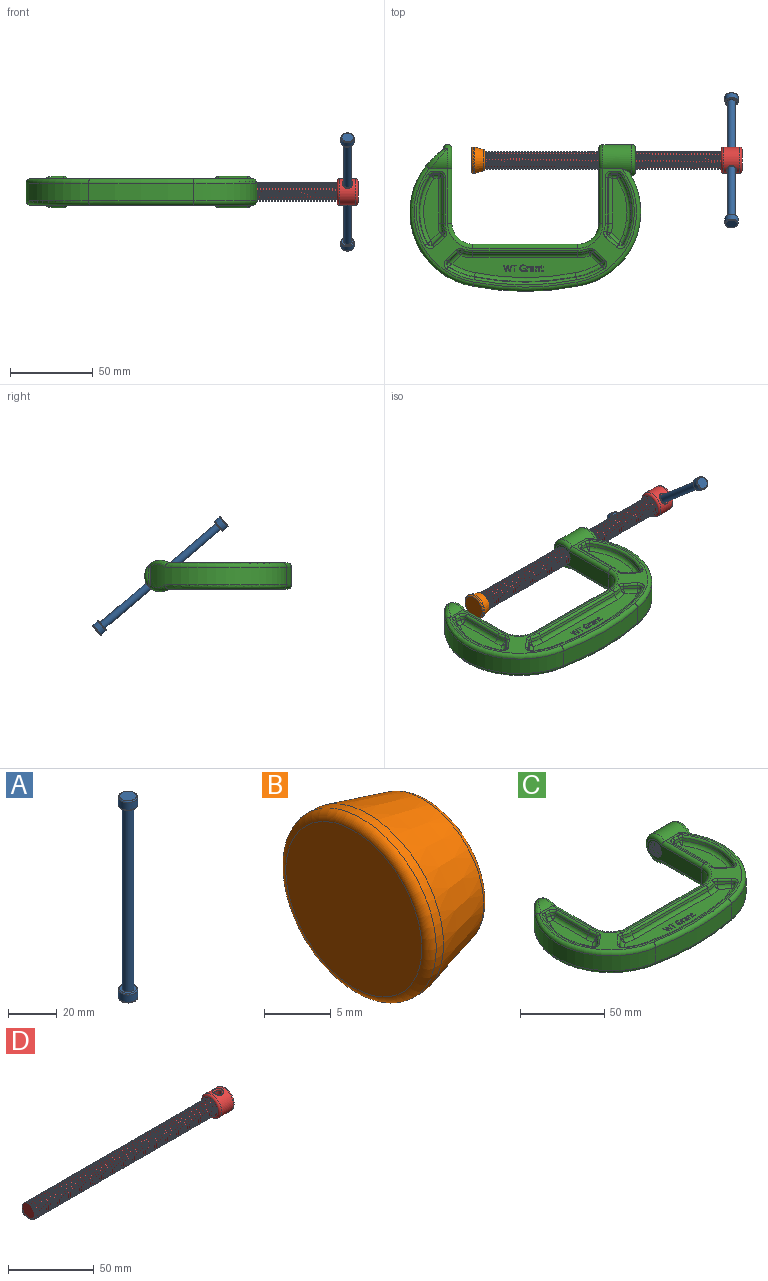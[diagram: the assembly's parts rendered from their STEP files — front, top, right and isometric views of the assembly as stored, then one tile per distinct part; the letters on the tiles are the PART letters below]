
ASSEMBLY  parts=4 mates=5
PART A: 11 faces, bbox 8.6x8.6x101.6 mm
  f0: cylinder r=2.37mm len=92.1mm, axis (0,0,-1), area 1374.3mm2, adj f2,f5
  f1: cylinder r=3.96mm len=7.93mm, axis (0,0,-1), area 93mm2, adj f9,f10
  f2: plane 6.91x6.91mm, normal (0,0,1), area 19.8mm2, adj f0,f10
  f3: plane 6.91x6.91mm, normal (0,0,-1), area 37.5mm2, adj f9
  f4: cylinder r=3.96mm len=7.93mm, axis (0,0,1), area 93mm2, adj f7,f8
  f5: plane 6.91x6.91mm, normal (0,0,-1), area 19.8mm2, adj f0,f8
  f6: plane 6.91x6.91mm, normal (0,0,1), area 37.5mm2, adj f7
  f7: torus R=3.45mm, axis (0,0,1), area 18.9mm2, adj f4,f6
  f8: torus R=3.45mm, axis (0,0,1), area 18.9mm2, adj f4,f5
  f9: torus R=3.45mm, axis (0,0,1), area 18.9mm2, adj f1,f3
  f10: torus R=3.45mm, axis (0,0,-1), area 18.9mm2, adj f1,f2
PART B: 11 faces, bbox 8.6x17.4x17.4 mm
  f0: plane 11.55x11.55mm, normal (1,0,0), area 17.8mm2, adj f4,f5,f6,f7,f10
  f1: cone r=7.94mm half-angle=15deg, axis (-1,0,0), area 269.5mm2, adj f3,f10
  f2: plane 14.35x14.35mm, normal (-1,0,0), area 161.8mm2, adj f9
  f3: cylinder r=7.94mm len=15.88mm, axis (-1,0,0), area 38mm2, adj f1,f9
  f4: bspline ~12.85x11.13mm, area 103.4mm2, adj f0,f6,f7,f8
  f5: bspline ~12.85x11.13mm, area 103.5mm2, adj f0,f6,f7,f8
  f6: cylinder r=5.56mm len=11.13mm, axis (-1,0,0), area 80mm2, adj f0,f4,f5,f8
  f7: cylinder r=4.67mm len=9.35mm, axis (-1,0,0), area 71mm2, adj f0,f4,f5,f8
  f8: plane 10.62x10.49mm, normal (1,0,0), area 82.5mm2, adj f4,f5,f6,f7
  f9: torus R=7.18mm, axis (-1,0,0), area 57.6mm2, adj f2,f3
  f10: torus R=5.65mm, axis (-1,0,0), area 38.1mm2, adj f0,f1
PART C: 361 faces, bbox 147.4x103.2x20.9 mm
  f0: plane 45.34x14.23mm, normal (-1,0,0), area 415.1mm2, adj f2,f9,f14,f15,f123,f358,f359,f360
  f1: plane 14.21x14.2mm, normal (1,0,0), area 70.8mm2, adj f2,f25,f26,f358,f359,f360
  f2: cylinder r=4.67mm len=22.23mm, axis (1,0,0), area 296.6mm2, adj f0,f1,f359,f360
  f3: plane 88.74x13.27mm, normal (0,0,1), area 824mm2, adj f61,f62,f63,f66,f67,f70,f71,f72
  f4: cylinder r=9.53mm len=12.02mm, axis (1,0,0), area 66.9mm2, adj f12,f20,f21
  f5: cylinder r=45.32mm len=82.5mm, axis (0,0,-1), area 1193.7mm2, adj f7,f21,f22,f28,f128,f129
  f6: plane 45.09x13.97mm, normal (1,0,0), area 497.5mm2, adj f11,f19,f20,f127
  f7: cylinder r=160.34mm len=63.5mm, axis (0,0,-1), area 690mm2, adj f5,f8,f24,f131
  f8: cylinder r=45.32mm len=68.35mm, axis (0,0,-1), area 945.9mm2, adj f7,f13,f23,f26,f130
  f9: cylinder r=12.7mm len=12.7mm, axis (0,0,-1), area 215.4mm2, adj f0,f10,f16,f124
  f10: plane 63.5x10.8mm, normal (0,1,0), area 685.5mm2, adj f9,f11,f17,f125
  f11: cylinder r=12.7mm len=12.7mm, axis (0,0,-1), area 215.4mm2, adj f6,f10,f18,f126
  f12: plane 134.76x72.01mm, normal (0,0,1), area 940mm2, adj f4,f13,f15,f16,f17,f18,f19,f21
  f13: cylinder r=9.53mm len=19.05mm, axis (-1,0,0), area 732.8mm2, adj f8,f12,f14,f23,f25,f122,f130
  f14: torus R=6.99mm, axis (1,0,0), area 151.3mm2, adj f0,f13,f15,f123
  f15: cylinder r=2.54mm len=33.67mm, axis (0,1,0), area 132.7mm2, adj f0,f12,f14,f16
  f16: torus R=15.24mm, axis (0,0,1), area 85.4mm2, adj f9,f12,f15,f17
  f17: cylinder r=2.54mm len=63.5mm, axis (1,0,0), area 253.4mm2, adj f10,f12,f16,f18
  f18: torus R=15.24mm, axis (0,0,1), area 85.4mm2, adj f11,f12,f17,f19
  f19: cylinder r=2.54mm len=33.67mm, axis (0,-1,0), area 132.7mm2, adj f6,f12,f18,f20
  f20: torus R=6.99mm, axis (1,0,0), area 189.3mm2, adj f4,f6,f19,f27,f28,f121,f127,f132
  f21: bspline ~15.93x15.22mm, area 60.2mm2, adj f4,f5,f12,f22,f27
  f22: torus R=42.78mm, axis (0,0,1), area 369.7mm2, adj f5,f12,f21,f24
  f23: torus R=42.78mm, axis (0,0,1), area 356.8mm2, adj f8,f12,f13,f24
  f24: torus R=157.8mm, axis (0,0,1), area 253.8mm2, adj f7,f12,f22,f23
  f25: torus R=6.99mm, axis (-1,0,0), area 205.8mm2, adj f1,f13,f26
  f26: bspline ~5.9x2.94mm, area 9.7mm2, adj f1,f8,f25
  f27: bspline ~3.03x2.58mm, area 1.3mm2, adj f20,f21,f28
  f28: bspline ~11.88x1.72mm, area 18.8mm2, adj f5,f20,f27,f132
  f29: plane 27.76x1.74mm, normal (0.97,0,0.26), area 49.9mm2, adj f30,f37,f73,f104
  f30: cone r=17.78mm half-angle=15deg, axis (0,0,-1), area 9.6mm2, adj f29,f31,f75,f103
  f31: cone r=2.54mm half-angle=15deg, axis (0,0,1), area 4mm2, adj f30,f32,f77,f105
  f32: plane 6.61x6.13mm, normal (0.65,0.71,0.26), area 15.4mm2, adj f31,f33,f79,f107
  f33: cone r=2.54mm half-angle=15deg, axis (0,0,1), area 6.5mm2, adj f32,f34,f81,f109
  f34: cone r=40.24mm half-angle=15deg, axis (0,0,1), area 78.6mm2, adj f33,f35,f80,f111
  f35: cone r=2.54mm half-angle=15deg, axis (0,0,1), area 3.5mm2, adj f34,f36,f78,f110
  f36: plane 3.69x1.74mm, normal (0,-0.97,0.26), area 6.6mm2, adj f35,f37,f76,f108
  f37: cone r=2.54mm half-angle=15deg, axis (0,0,1), area 5.7mm2, adj f29,f36,f74,f106
  f38: plane 37.6x9.56mm, normal (0,0,1), area 258.8mm2, adj f73,f75,f76,f79,f80
  f39: cone r=17.78mm half-angle=15deg, axis (0,0,-1), area 12.3mm2, adj f40,f50,f62,f91
  f40: cone r=2.54mm half-angle=15deg, axis (0,0,1), area 4mm2, adj f39,f41,f64,f92
  f41: plane 6.61x6.13mm, normal (0.65,-0.71,0.26), area 15.4mm2, adj f40,f42,f66,f94
  f42: cone r=2.54mm half-angle=15deg, axis (0,0,1), area 6.5mm2, adj f41,f43,f68,f96
  f43: cone r=40.24mm half-angle=15deg, axis (0,0,1), area 30.8mm2, adj f42,f44,f70,f98
  f44: cone r=155.26mm half-angle=15deg, axis (0,0,1), area 111.4mm2, adj f43,f45,f72,f100
  f45: cone r=40.24mm half-angle=15deg, axis (0,0,1), area 30.8mm2, adj f44,f46,f71,f102
  f46: cone r=2.54mm half-angle=15deg, axis (0,0,1), area 6.5mm2, adj f45,f47,f69,f101
  f47: plane 6.61x6.13mm, normal (-0.65,-0.71,0.26), area 15.4mm2, adj f46,f48,f67,f99
  f48: cone r=2.54mm half-angle=15deg, axis (0,0,1), area 4mm2, adj f47,f49,f65,f97
  f49: cone r=17.78mm half-angle=15deg, axis (0,0,-1), area 12.3mm2, adj f48,f50,f63,f95
  f50: plane 63.5x1.74mm, normal (0,-0.97,0.26), area 114.2mm2, adj f39,f49,f61,f93
  f51: plane 27.76x1.74mm, normal (-0.97,0,0.26), area 49.9mm2, adj f52,f59,f90,f120
  f52: cone r=2.54mm half-angle=15deg, axis (0,0,1), area 5.7mm2, adj f51,f53,f89,f119
  f53: plane 3.69x1.74mm, normal (0,-0.97,0.26), area 6.6mm2, adj f52,f54,f87,f117
  f54: cone r=2.54mm half-angle=15deg, axis (0,0,1), area 3.5mm2, adj f53,f55,f85,f115
  f55: cone r=40.24mm half-angle=15deg, axis (0,0,1), area 78.6mm2, adj f54,f56,f83,f113
  f56: cone r=2.54mm half-angle=15deg, axis (0,0,1), area 6.5mm2, adj f55,f57,f82,f112
  f57: plane 6.61x6.13mm, normal (-0.65,0.71,0.26), area 15.4mm2, adj f56,f58,f84,f114
  f58: cone r=2.54mm half-angle=15deg, axis (0,0,1), area 4mm2, adj f57,f59,f86,f116
  f59: cone r=17.78mm half-angle=15deg, axis (0,0,-1), area 9.6mm2, adj f51,f58,f88,f118
  f60: plane 37.6x9.56mm, normal (0,0,1), area 258.8mm2, adj f83,f84,f87,f88,f90
  f61: cylinder r=2.54mm len=63.5mm, axis (-1,0,0), area 211.1mm2, adj f3,f50,f62,f63
  f62: torus R=21mm, axis (0,0,1), area 23.7mm2, adj f3,f39,f61,f64
  f63: torus R=21mm, axis (0,0,1), area 23.7mm2, adj f3,f49,f61,f65
  f64: bspline ~2.55x1.88mm, area 2.4mm2, adj f40,f62,f66
  f65: bspline ~2.55x1.88mm, area 2.4mm2, adj f48,f63,f67
  f66: cylinder r=2.54mm len=7.96mm, axis (-0.74,-0.68,0), area 26.3mm2, adj f3,f41,f64,f68
  f67: cylinder r=2.54mm len=7.96mm, axis (0.74,-0.68,0), area 26.3mm2, adj f3,f47,f65,f69
  f68: bspline ~2.81x2.78mm, area 3.9mm2, adj f42,f66,f70
  f69: bspline ~2.81x2.78mm, area 3.9mm2, adj f46,f67,f71
  f70: torus R=37.02mm, axis (0,0,1), area 53.8mm2, adj f3,f43,f68,f72
  f71: torus R=37.02mm, axis (0,0,1), area 53.8mm2, adj f3,f45,f69,f72
  f72: torus R=152.04mm, axis (0,0,1), area 204.4mm2, adj f3,f44,f70,f71
  f73: cylinder r=2.54mm len=27.76mm, axis (0,-1,0), area 91.1mm2, adj f29,f38,f74,f75
  f74: bspline ~2.45x2.45mm, area 3.4mm2, adj f37,f73,f76
  f75: torus R=21mm, axis (0,0,1), area 18.2mm2, adj f30,f38,f73,f77
  f76: cylinder r=2.54mm len=3.69mm, axis (1,0,0), area 10.5mm2, adj f36,f38,f74,f78
  f77: bspline ~2.53x1.88mm, area 2.4mm2, adj f31,f75,f79
  f78: bspline ~2.45x1.88mm, area 2.1mm2, adj f35,f76,f80
  f79: cylinder r=2.54mm len=7.96mm, axis (0.74,-0.68,0), area 26.3mm2, adj f32,f38,f77,f81
  f80: torus R=37.02mm, axis (0,0,1), area 138.6mm2, adj f34,f38,f78,f81
  f81: bspline ~2.8x2.75mm, area 4mm2, adj f33,f79,f80
  f82: bspline ~2.8x2.75mm, area 3.9mm2, adj f56,f83,f84
  f83: torus R=37.02mm, axis (0,0,1), area 138.6mm2, adj f55,f60,f82,f85
  f84: cylinder r=2.54mm len=7.96mm, axis (-0.74,-0.68,0), area 26.3mm2, adj f57,f60,f82,f86
  f85: bspline ~2.45x1.88mm, area 2.1mm2, adj f54,f83,f87
  f86: bspline ~2.53x1.88mm, area 2.4mm2, adj f58,f84,f88
  f87: cylinder r=2.54mm len=3.69mm, axis (1,0,0), area 10.5mm2, adj f53,f60,f85,f89
  f88: torus R=21mm, axis (0,0,1), area 18.2mm2, adj f59,f60,f86,f90
  f89: bspline ~2.45x2.45mm, area 3.4mm2, adj f52,f87,f90
  f90: cylinder r=2.54mm len=27.76mm, axis (0,1,0), area 91.1mm2, adj f51,f60,f88,f89
  f91: torus R=16.61mm, axis (0,0,1), area 13mm2, adj f12,f39,f92,f93
  f92: torus R=3.71mm, axis (0,0,1), area 6.3mm2, adj f12,f40,f91,f94
  f93: cylinder r=1.52mm len=63.5mm, axis (1,0,0), area 126.7mm2, adj f12,f50,f91,f95
  f94: cylinder r=1.52mm len=7.29mm, axis (0.74,0.68,0), area 17.1mm2, adj f12,f41,f92,f96
  f95: torus R=16.61mm, axis (0,0,1), area 13mm2, adj f12,f49,f93,f97
  f96: torus R=3.71mm, axis (0,0,1), area 10.3mm2, adj f12,f42,f94,f98
  f97: torus R=3.71mm, axis (0,0,1), area 6.3mm2, adj f12,f48,f95,f99
  f98: torus R=41.41mm, axis (0,0,1), area 34.9mm2, adj f12,f43,f96,f100
  f99: cylinder r=1.52mm len=7.29mm, axis (-0.74,0.68,0), area 17.1mm2, adj f12,f47,f97,f101
  f100: torus R=156.43mm, axis (0,0,1), area 124.1mm2, adj f12,f44,f98,f102
  f101: torus R=3.71mm, axis (0,0,1), area 10.3mm2, adj f12,f46,f99,f102
  f102: torus R=41.41mm, axis (0,0,1), area 34.9mm2, adj f12,f45,f100,f101
  f103: torus R=16.61mm, axis (0,0,1), area 10.1mm2, adj f12,f30,f104,f105
  f104: cylinder r=1.52mm len=27.76mm, axis (0,1,0), area 55.4mm2, adj f12,f29,f103,f106
  f105: torus R=3.71mm, axis (0,0,1), area 6.3mm2, adj f12,f31,f103,f107
  f106: torus R=3.71mm, axis (0,0,1), area 8.9mm2, adj f12,f37,f104,f108
  f107: cylinder r=1.52mm len=7.29mm, axis (-0.74,0.68,0), area 17.1mm2, adj f12,f32,f105,f109
  f108: cylinder r=1.52mm len=3.69mm, axis (-1,0,0), area 7.4mm2, adj f12,f36,f106,f110
  f109: torus R=3.71mm, axis (0,0,1), area 10.3mm2, adj f12,f33,f107,f111
  f110: torus R=3.71mm, axis (0,0,1), area 5.5mm2, adj f12,f35,f108,f111
  f111: torus R=41.41mm, axis (0,0,1), area 89mm2, adj f12,f34,f109,f110
  f112: torus R=3.71mm, axis (0,0,1), area 10.3mm2, adj f12,f56,f113,f114
  f113: torus R=41.41mm, axis (0,0,1), area 89mm2, adj f12,f55,f112,f115
  f114: cylinder r=1.52mm len=7.29mm, axis (0.74,0.68,0), area 17.1mm2, adj f12,f57,f112,f116
  f115: torus R=3.71mm, axis (0,0,1), area 5.5mm2, adj f12,f54,f113,f117
  f116: torus R=3.71mm, axis (0,0,1), area 6.3mm2, adj f12,f58,f114,f118
  f117: cylinder r=1.52mm len=3.69mm, axis (-1,0,0), area 7.4mm2, adj f12,f53,f115,f119
  f118: torus R=16.61mm, axis (0,0,1), area 10.1mm2, adj f12,f59,f116,f120
  f119: torus R=3.71mm, axis (0,0,1), area 8.9mm2, adj f12,f52,f117,f120
  f120: cylinder r=1.52mm len=27.76mm, axis (0,-1,0), area 55.4mm2, adj f12,f51,f118,f119
  f121: cylinder r=9.53mm len=12.02mm, axis (1,0,0), area 66.9mm2, adj f20,f122,f128
  f122: plane 134.76x72.01mm, normal (0,0,-1), area 940mm2, adj f13,f121,f123,f124,f125,f126,f127,f128
  f123: cylinder r=2.54mm len=33.67mm, axis (0,1,0), area 132.7mm2, adj f0,f14,f122,f124
  f124: torus R=15.24mm, axis (0,0,-1), area 85.4mm2, adj f9,f122,f123,f125
  f125: cylinder r=2.54mm len=63.5mm, axis (1,0,0), area 253.4mm2, adj f10,f122,f124,f126
  f126: torus R=15.24mm, axis (0,0,-1), area 85.4mm2, adj f11,f122,f125,f127
  f127: cylinder r=2.54mm len=33.67mm, axis (0,-1,0), area 132.7mm2, adj f6,f20,f122,f126
  f128: bspline ~15.93x15.22mm, area 60.2mm2, adj f5,f121,f122,f129,f132
  f129: torus R=42.78mm, axis (0,0,-1), area 369.7mm2, adj f5,f122,f128,f131
  f130: torus R=42.78mm, axis (0,0,-1), area 356.8mm2, adj f8,f13,f122,f131
  f131: torus R=157.8mm, axis (0,0,-1), area 253.8mm2, adj f7,f122,f129,f130
  f132: bspline ~3.03x2.58mm, area 1.3mm2, adj f20,f28,f128
  f133: plane 27.76x1.74mm, normal (0.97,0,-0.26), area 49.9mm2, adj f134,f141,f178,f209
  f134: cone r=17.78mm half-angle=15deg, axis (0,0,1), area 9.6mm2, adj f133,f135,f180,f208
  f135: cone r=2.54mm half-angle=15deg, axis (0,0,-1), area 4mm2, adj f134,f136,f182,f210
  f136: plane 6.61x6.13mm, normal (0.65,0.71,-0.26), area 15.4mm2, adj f135,f137,f184,f212
  f137: cone r=2.54mm half-angle=15deg, axis (0,0,-1), area 6.5mm2, adj f136,f138,f186,f214
  f138: cone r=40.24mm half-angle=15deg, axis (0,0,-1), area 78.6mm2, adj f137,f139,f185,f216
  f139: cone r=2.54mm half-angle=15deg, axis (0,0,-1), area 3.5mm2, adj f138,f140,f183,f215
  f140: plane 3.69x1.74mm, normal (0,-0.97,-0.26), area 6.6mm2, adj f139,f141,f181,f213
  f141: cone r=2.54mm half-angle=15deg, axis (0,0,-1), area 5.7mm2, adj f133,f140,f179,f211
  f142: plane 37.6x9.56mm, normal (0,0,-1), area 258.8mm2, adj f178,f180,f181,f184,f185
  f143: cone r=17.78mm half-angle=15deg, axis (0,0,1), area 12.3mm2, adj f144,f154,f167,f196
  f144: cone r=2.54mm half-angle=15deg, axis (0,0,-1), area 4mm2, adj f143,f145,f169,f197
  f145: plane 6.61x6.13mm, normal (0.65,-0.71,-0.26), area 15.4mm2, adj f144,f146,f171,f199
  f146: cone r=2.54mm half-angle=15deg, axis (0,0,-1), area 6.5mm2, adj f145,f147,f173,f201
  f147: cone r=40.24mm half-angle=15deg, axis (0,0,-1), area 30.8mm2, adj f146,f148,f175,f203
  f148: cone r=155.26mm half-angle=15deg, axis (0,0,-1), area 111.4mm2, adj f147,f149,f177,f205
  f149: cone r=40.24mm half-angle=15deg, axis (0,0,-1), area 30.8mm2, adj f148,f150,f176,f207
  f150: cone r=2.54mm half-angle=15deg, axis (0,0,-1), area 6.5mm2, adj f149,f151,f174,f206
  f151: plane 6.61x6.13mm, normal (-0.65,-0.71,-0.26), area 15.4mm2, adj f150,f152,f172,f204
  f152: cone r=2.54mm half-angle=15deg, axis (0,0,-1), area 4mm2, adj f151,f153,f170,f202
  f153: cone r=17.78mm half-angle=15deg, axis (0,0,1), area 12.3mm2, adj f152,f154,f168,f200
  f154: plane 63.5x1.74mm, normal (0,-0.97,-0.26), area 114.2mm2, adj f143,f153,f166,f198
  f155: plane 88.74x13.27mm, normal (0,0,-1), area 849.9mm2, adj f166,f167,f168,f171,f172,f175,f176,f177
  f156: plane 27.76x1.74mm, normal (-0.97,0,-0.26), area 49.9mm2, adj f157,f164,f195,f225
  f157: cone r=2.54mm half-angle=15deg, axis (0,0,-1), area 5.7mm2, adj f156,f158,f194,f224
  f158: plane 3.69x1.74mm, normal (0,-0.97,-0.26), area 6.6mm2, adj f157,f159,f192,f222
  f159: cone r=2.54mm half-angle=15deg, axis (0,0,-1), area 3.5mm2, adj f158,f160,f190,f220
  f160: cone r=40.24mm half-angle=15deg, axis (0,0,-1), area 78.6mm2, adj f159,f161,f188,f218
  f161: cone r=2.54mm half-angle=15deg, axis (0,0,-1), area 6.5mm2, adj f160,f162,f187,f217
  f162: plane 6.61x6.13mm, normal (-0.65,0.71,-0.26), area 15.4mm2, adj f161,f163,f189,f219
  f163: cone r=2.54mm half-angle=15deg, axis (0,0,-1), area 4mm2, adj f162,f164,f191,f221
  f164: cone r=17.78mm half-angle=15deg, axis (0,0,1), area 9.6mm2, adj f156,f163,f193,f223
  f165: plane 37.6x9.56mm, normal (0,0,-1), area 258.8mm2, adj f188,f189,f192,f193,f195
  f166: cylinder r=2.54mm len=63.5mm, axis (-1,0,0), area 211.1mm2, adj f154,f155,f167,f168
  f167: torus R=21mm, axis (0,0,-1), area 23.7mm2, adj f143,f155,f166,f169
  f168: torus R=21mm, axis (0,0,-1), area 23.7mm2, adj f153,f155,f166,f170
  f169: bspline ~2.55x1.88mm, area 2.4mm2, adj f144,f167,f171
  f170: bspline ~2.55x1.88mm, area 2.4mm2, adj f152,f168,f172
  f171: cylinder r=2.54mm len=7.96mm, axis (-0.74,-0.68,0), area 26.3mm2, adj f145,f155,f169,f173
  f172: cylinder r=2.54mm len=7.96mm, axis (0.74,-0.68,0), area 26.3mm2, adj f151,f155,f170,f174
  f173: bspline ~2.81x2.78mm, area 3.9mm2, adj f146,f171,f175
  f174: bspline ~2.81x2.78mm, area 3.9mm2, adj f150,f172,f176
  f175: torus R=37.02mm, axis (0,0,-1), area 53.8mm2, adj f147,f155,f173,f177
  f176: torus R=37.02mm, axis (0,0,-1), area 53.8mm2, adj f149,f155,f174,f177
  f177: torus R=152.04mm, axis (0,0,-1), area 204.4mm2, adj f148,f155,f175,f176
  f178: cylinder r=2.54mm len=27.76mm, axis (0,-1,0), area 91.1mm2, adj f133,f142,f179,f180
  f179: bspline ~2.45x2.45mm, area 3.4mm2, adj f141,f178,f181
  f180: torus R=21mm, axis (0,0,-1), area 18.2mm2, adj f134,f142,f178,f182
  f181: cylinder r=2.54mm len=3.69mm, axis (1,0,0), area 10.5mm2, adj f140,f142,f179,f183
  f182: bspline ~2.53x1.88mm, area 2.4mm2, adj f135,f180,f184
  f183: bspline ~2.45x1.88mm, area 2.1mm2, adj f139,f181,f185
  f184: cylinder r=2.54mm len=7.96mm, axis (0.74,-0.68,0), area 26.3mm2, adj f136,f142,f182,f186
  f185: torus R=37.02mm, axis (0,0,-1), area 138.6mm2, adj f138,f142,f183,f186
  f186: bspline ~2.8x2.75mm, area 4mm2, adj f137,f184,f185
  f187: bspline ~2.8x2.75mm, area 3.9mm2, adj f161,f188,f189
  f188: torus R=37.02mm, axis (0,0,-1), area 138.6mm2, adj f160,f165,f187,f190
  f189: cylinder r=2.54mm len=7.96mm, axis (-0.74,-0.68,0), area 26.3mm2, adj f162,f165,f187,f191
  f190: bspline ~2.45x1.88mm, area 2.1mm2, adj f159,f188,f192
  f191: bspline ~2.53x1.88mm, area 2.4mm2, adj f163,f189,f193
  f192: cylinder r=2.54mm len=3.69mm, axis (1,0,0), area 10.5mm2, adj f158,f165,f190,f194
  f193: torus R=21mm, axis (0,0,-1), area 18.2mm2, adj f164,f165,f191,f195
  f194: bspline ~2.45x2.45mm, area 3.4mm2, adj f157,f192,f195
  f195: cylinder r=2.54mm len=27.76mm, axis (0,1,0), area 91.1mm2, adj f156,f165,f193,f194
  f196: torus R=16.61mm, axis (0,0,-1), area 13mm2, adj f122,f143,f197,f198
  f197: torus R=3.71mm, axis (0,0,-1), area 6.3mm2, adj f122,f144,f196,f199
  f198: cylinder r=1.52mm len=63.5mm, axis (1,0,0), area 126.7mm2, adj f122,f154,f196,f200
  f199: cylinder r=1.52mm len=7.29mm, axis (0.74,0.68,0), area 17.1mm2, adj f122,f145,f197,f201
  f200: torus R=16.61mm, axis (0,0,-1), area 13mm2, adj f122,f153,f198,f202
  f201: torus R=3.71mm, axis (0,0,-1), area 10.3mm2, adj f122,f146,f199,f203
  f202: torus R=3.71mm, axis (0,0,-1), area 6.3mm2, adj f122,f152,f200,f204
  f203: torus R=41.41mm, axis (0,0,-1), area 34.9mm2, adj f122,f147,f201,f205
  f204: cylinder r=1.52mm len=7.29mm, axis (-0.74,0.68,0), area 17.1mm2, adj f122,f151,f202,f206
  f205: torus R=156.43mm, axis (0,0,-1), area 124.1mm2, adj f122,f148,f203,f207
  f206: torus R=3.71mm, axis (0,0,-1), area 10.3mm2, adj f122,f150,f204,f207
  f207: torus R=41.41mm, axis (0,0,-1), area 34.9mm2, adj f122,f149,f205,f206
  f208: torus R=16.61mm, axis (0,0,-1), area 10.1mm2, adj f122,f134,f209,f210
  f209: cylinder r=1.52mm len=27.76mm, axis (0,1,0), area 55.4mm2, adj f122,f133,f208,f211
  f210: torus R=3.71mm, axis (0,0,-1), area 6.3mm2, adj f122,f135,f208,f212
  f211: torus R=3.71mm, axis (0,0,-1), area 8.9mm2, adj f122,f141,f209,f213
  f212: cylinder r=1.52mm len=7.29mm, axis (-0.74,0.68,0), area 17.1mm2, adj f122,f136,f210,f214
  f213: cylinder r=1.52mm len=3.69mm, axis (-1,0,0), area 7.4mm2, adj f122,f140,f211,f215
  f214: torus R=3.71mm, axis (0,0,-1), area 10.3mm2, adj f122,f137,f212,f216
  f215: torus R=3.71mm, axis (0,0,-1), area 5.5mm2, adj f122,f139,f213,f216
  f216: torus R=41.41mm, axis (0,0,-1), area 89mm2, adj f122,f138,f214,f215
  f217: torus R=3.71mm, axis (0,0,-1), area 10.3mm2, adj f122,f161,f218,f219
  f218: torus R=41.41mm, axis (0,0,-1), area 89mm2, adj f122,f160,f217,f220
  f219: cylinder r=1.52mm len=7.29mm, axis (0.74,0.68,0), area 17.1mm2, adj f122,f162,f217,f221
  f220: torus R=3.71mm, axis (0,0,-1), area 5.5mm2, adj f122,f159,f218,f222
  f221: torus R=3.71mm, axis (0,0,-1), area 6.3mm2, adj f122,f163,f219,f223
  f222: cylinder r=1.52mm len=3.69mm, axis (-1,0,0), area 7.4mm2, adj f122,f158,f220,f224
  f223: torus R=16.61mm, axis (0,0,-1), area 10.1mm2, adj f122,f164,f221,f225
  f224: torus R=3.71mm, axis (0,0,-1), area 8.9mm2, adj f122,f157,f222,f225
  f225: cylinder r=1.52mm len=27.76mm, axis (0,-1,0), area 55.4mm2, adj f122,f156,f223,f224
  f226: plane 0.76x0.46mm, normal (0,1,0), area 0.3mm2, adj f3,f227,f233,f234
  f227: plane 3.52x0.76mm, normal (-1,0,0), area 2.7mm2, adj f3,f226,f228,f234
  f228: plane 1.24x0.76mm, normal (0,1,0), area 0.9mm2, adj f3,f227,f229,f234
  f229: plane 0.76x0.41mm, normal (-1,0,0), area 0.3mm2, adj f3,f228,f230,f234
  f230: plane 2.94x0.76mm, normal (0,-1,0), area 2.2mm2, adj f3,f229,f231,f234
  f231: plane 0.76x0.41mm, normal (1,0,0), area 0.3mm2, adj f3,f230,f232,f234
  f232: plane 1.24x0.76mm, normal (0,1,0), area 0.9mm2, adj f3,f231,f233,f234
  f233: plane 3.52x0.76mm, normal (1,0,0), area 2.7mm2, adj f3,f226,f232,f234
  f234: plane 3.92x2.94mm, normal (0,0,1), area 2.8mm2, adj f226,f227,f228,f229,f230,f231,f232,f233
  f235: plane 1.33x0.76mm, normal (0,-1,0), area 1mm2, adj f3,f236,f254,f255
  f236: plane 0.76x0.41mm, normal (1,0,0), area 0.3mm2, adj f3,f235,f237,f255
  f237: plane 0.88x0.76mm, normal (0,1,0), area 0.7mm2, adj f3,f236,f238,f255
  f238: plane 1.21x0.76mm, normal (1,0,0), area 0.9mm2, adj f3,f237,f239,f255
  f239: extruded ~0.8x0.76mm, area 0.6mm2, adj f3,f238,f240,f255
  f240: extruded ~1.14x0.76mm, area 0.9mm2, adj f3,f239,f241,f255
  f241: extruded ~1.2x0.76mm, area 1mm2, adj f3,f240,f242,f255
  f242: extruded ~1.18x0.76mm, area 1mm2, adj f3,f241,f243,f255
  f243: extruded ~1.12x0.76mm, area 0.9mm2, adj f3,f242,f244,f255
  f244: extruded ~1.02x0.76mm, area 0.8mm2, adj f3,f243,f245,f255
  f245: plane 0.76x0.4mm, normal (-0.92,0.4,0), area 0.3mm2, adj f3,f244,f246,f255
  f246: extruded ~1.17x0.76mm, area 0.9mm2, adj f3,f245,f247,f255
  f247: extruded ~1.08x0.76mm, area 0.9mm2, adj f3,f246,f248,f255
  f248: extruded ~0.76x0.71mm, area 0.8mm2, adj f3,f247,f249,f255
  f249: extruded ~1.07x0.76mm, area 0.8mm2, adj f3,f248,f250,f255
  f250: extruded ~1.49x0.76mm, area 1.2mm2, adj f3,f249,f251,f255
  f251: extruded ~1.39x0.76mm, area 1.2mm2, adj f3,f250,f252,f255
  f252: extruded ~0.76x0.75mm, area 0.6mm2, adj f3,f251,f253,f255
  f253: extruded ~0.76x0.63mm, area 0.5mm2, adj f3,f252,f254,f255
  f254: plane 1.91x0.76mm, normal (-1,0,0), area 1.5mm2, adj f3,f235,f253,f255
  f255: plane 4.03x3.26mm, normal (0,0,1), area 4.7mm2, adj f235,f236,f237,f238,f239,f240,f241,f242
  f256: extruded ~0.76x0.35mm, area 0.3mm2, adj f3,f257,f268,f269
  f257: extruded ~0.76x0.51mm, area 0.4mm2, adj f3,f256,f258,f269
  f258: extruded ~0.76x0.44mm, area 0.5mm2, adj f3,f257,f259,f269
  f259: plane 0.76x0.02mm, normal (0,-1,0), area 0mm2, adj f3,f258,f260,f269
  f260: plane 0.76x0.54mm, normal (-1,-0.09,0), area 0.4mm2, adj f3,f259,f261,f269
  f261: plane 0.76x0.37mm, normal (0,-1,0), area 0.3mm2, adj f3,f260,f262,f269
  f262: plane 2.94x0.76mm, normal (1,0,0), area 2.2mm2, adj f3,f261,f263,f269
  f263: plane 0.76x0.45mm, normal (0,1,0), area 0.3mm2, adj f3,f262,f264,f269
  f264: plane 1.58x0.76mm, normal (-1,0,0), area 1.2mm2, adj f3,f263,f265,f269
  f265: extruded ~0.76x0.72mm, area 0.6mm2, adj f3,f264,f266,f269
  f266: extruded ~0.76x0.61mm, area 0.5mm2, adj f3,f265,f267,f269
  f267: extruded ~0.76x0.32mm, area 0.2mm2, adj f3,f266,f268,f269
  f268: plane 0.76x0.41mm, normal (-0.99,0.15,0), area 0.3mm2, adj f3,f256,f267,f269
  f269: plane 2.99x1.69mm, normal (0,0,1), area 1.8mm2, adj f256,f257,f258,f259,f260,f261,f262,f263
  f270: plane 1.9x0.76mm, normal (1,0,0), area 1.4mm2, adj f3,f271,f286,f287
  f271: plane 0.76x0.45mm, normal (0,1,0), area 0.3mm2, adj f3,f270,f272,f287
  f272: plane 1.92x0.76mm, normal (-1,0,0), area 1.5mm2, adj f3,f271,f273,f287
  f273: extruded ~0.82x0.76mm, area 0.7mm2, adj f3,f272,f274,f287
  f274: extruded ~0.8x0.76mm, area 0.7mm2, adj f3,f273,f275,f287
  f275: extruded ~0.76x0.55mm, area 0.4mm2, adj f3,f274,f276,f287
  f276: extruded ~0.76x0.38mm, area 0.4mm2, adj f3,f275,f277,f287
  f277: plane 0.76x0.02mm, normal (0,-1,0), area 0mm2, adj f3,f276,f278,f287
  f278: plane 0.76x0.4mm, normal (-0.98,-0.18,0), area 0.3mm2, adj f3,f277,f279,f287
  f279: plane 0.76x0.36mm, normal (0,-1,0), area 0.3mm2, adj f3,f278,f280,f287
  f280: plane 2.94x0.76mm, normal (1,0,0), area 2.2mm2, adj f3,f279,f281,f287
  f281: plane 0.76x0.45mm, normal (0,1,0), area 0.3mm2, adj f3,f280,f282,f287
  f282: plane 1.54x0.76mm, normal (-1,0,0), area 1.2mm2, adj f3,f281,f283,f287
  f283: extruded ~0.82x0.76mm, area 0.7mm2, adj f3,f282,f284,f287
  f284: extruded ~0.76x0.68mm, area 0.6mm2, adj f3,f283,f285,f287
  f285: extruded ~0.76x0.51mm, area 0.4mm2, adj f3,f284,f286,f287
  f286: extruded ~0.76x0.54mm, area 0.4mm2, adj f3,f270,f285,f287
  f287: plane 2.99x2.46mm, normal (0,0,1), area 3.1mm2, adj f270,f271,f272,f273,f274,f275,f276,f277
  f288: extruded ~0.76x0.23mm, area 0.2mm2, adj f3,f289,f306,f307
  f289: extruded ~0.76x0.35mm, area 0.3mm2, adj f3,f288,f290,f307
  f290: extruded ~0.76x0.41mm, area 0.3mm2, adj f3,f289,f291,f307
  f291: plane 1.73x0.76mm, normal (-1,0,0), area 1.3mm2, adj f3,f290,f292,f307
  f292: plane 0.85x0.76mm, normal (0,1,0), area 0.7mm2, adj f3,f291,f293,f307
  f293: plane 0.76x0.35mm, normal (-1,0,0), area 0.3mm2, adj f3,f292,f294,f307
  f294: plane 0.85x0.76mm, normal (0,-1,0), area 0.7mm2, adj f3,f293,f295,f307
  f295: plane 0.76x0.68mm, normal (-1,0,0), area 0.5mm2, adj f3,f294,f296,f307
  f296: plane 0.76x0.26mm, normal (0,-1,0), area 0.2mm2, adj f3,f295,f297,f307
  f297: plane 0.76x0.63mm, normal (0.96,-0.29,0), area 0.5mm2, adj f3,f296,f298,f307
  f298: plane 0.76x0.42mm, normal (0.4,-0.92,0), area 0.4mm2, adj f3,f297,f299,f307
  f299: plane 0.76x0.21mm, normal (1,0,0), area 0.2mm2, adj f3,f298,f300,f307
  f300: plane 0.76x0.42mm, normal (0,1,0), area 0.3mm2, adj f3,f299,f301,f307
  f301: plane 1.75x0.76mm, normal (1,0,0), area 1.3mm2, adj f3,f300,f302,f307
  f302: extruded ~0.9x0.85mm, area 1.1mm2, adj f3,f301,f303,f307
  f303: extruded ~0.76x0.25mm, area 0.2mm2, adj f3,f302,f304,f307
  f304: extruded ~0.76x0.21mm, area 0.2mm2, adj f3,f303,f305,f307
  f305: plane 0.76x0.34mm, normal (-1,0,0), area 0.3mm2, adj f3,f304,f306,f307
  f306: extruded ~0.76x0.17mm, area 0.1mm2, adj f3,f288,f305,f307
  f307: plane 3.68x1.74mm, normal (0,0,1), area 2.2mm2, adj f288,f289,f290,f291,f292,f293,f294,f295
  f308: extruded ~0.76x0.65mm, area 0.5mm2, adj f309,f334,f335,f357
  f309: extruded ~0.76x0.41mm, area 0.3mm2, adj f308,f310,f335,f357
  f310: extruded ~0.76x0.37mm, area 0.3mm2, adj f309,f311,f335,f357
  f311: extruded ~0.76x0.45mm, area 0.4mm2, adj f310,f312,f335,f357
  f312: extruded ~0.77x0.76mm, area 0.6mm2, adj f311,f313,f335,f357
  f313: plane 0.76x0.45mm, normal (-0.04,1,0), area 0.3mm2, adj f312,f314,f335,f357
  f314: plane 0.76x0.27mm, normal (1,0,0), area 0.2mm2, adj f313,f334,f335,f357
  f315: plane 0.76x0.42mm, normal (0.98,0.21,0), area 0.3mm2, adj f3,f316,f333,f335
  f316: plane 0.76x0.33mm, normal (0,1,0), area 0.3mm2, adj f3,f315,f317,f335
  f317: plane 2.01x0.76mm, normal (-1,0,0), area 1.5mm2, adj f3,f316,f318,f335
  f318: extruded ~0.76x0.75mm, area 0.6mm2, adj f3,f317,f319,f335
  f319: extruded ~0.78x0.76mm, area 0.6mm2, adj f3,f318,f320,f335
  f320: extruded ~0.76x0.52mm, area 0.4mm2, adj f3,f319,f321,f335
  f321: extruded ~0.76x0.48mm, area 0.4mm2, adj f3,f320,f322,f335
  f322: plane 0.76x0.34mm, normal (0.93,0.37,0), area 0.3mm2, adj f3,f321,f323,f335
  f323: extruded ~0.83x0.76mm, area 0.7mm2, adj f3,f322,f324,f335
  f324: extruded ~0.76x0.48mm, area 0.4mm2, adj f3,f323,f325,f335
  f325: extruded ~0.76x0.51mm, area 0.4mm2, adj f3,f324,f326,f335
  f326: plane 0.76x0.18mm, normal (1,0,0), area 0.1mm2, adj f3,f325,f327,f335
  f327: plane 0.76x0.5mm, normal (0.03,-1,0), area 0.4mm2, adj f3,f326,f328,f335
  f328: extruded ~1.42x0.93mm, area 1.5mm2, adj f3,f327,f329,f335
  f329: extruded ~0.76x0.64mm, area 0.5mm2, adj f3,f328,f330,f335
  f330: extruded ~0.76x0.69mm, area 0.6mm2, adj f3,f329,f331,f335
  f331: extruded ~0.76x0.55mm, area 0.4mm2, adj f3,f330,f332,f335
  f332: extruded ~0.76x0.44mm, area 0.4mm2, adj f3,f331,f333,f335
  f333: plane 0.76x0.02mm, normal (0,1,0), area 0mm2, adj f3,f315,f332,f335
  f334: extruded ~0.76x0.64mm, area 0.5mm2, adj f308,f314,f335,f357
  f335: plane 3.04x2.36mm, normal (0,0,1), area 3.4mm2, adj f308,f309,f310,f311,f312,f313,f314,f315
  f336: plane 0.76x0.45mm, normal (0,1,0), area 0.3mm2, adj f3,f337,f355,f356
  f337: plane 3.92x1.05mm, normal (-0.97,0.26,0), area 3.1mm2, adj f3,f336,f338,f356
  f338: plane 0.76x0.48mm, normal (0,-1,0), area 0.4mm2, adj f3,f337,f339,f356
  f339: plane 2.42x0.76mm, normal (0.97,-0.25,0), area 1.9mm2, adj f3,f338,f340,f356
  f340: extruded ~0.93x0.76mm, area 0.7mm2, adj f3,f339,f341,f356
  f341: extruded ~0.94x0.76mm, area 0.7mm2, adj f3,f340,f342,f356
  f342: plane 2.41x0.76mm, normal (-0.96,-0.29,0), area 1.9mm2, adj f3,f341,f343,f356
  f343: plane 0.76x0.48mm, normal (0,-1,0), area 0.4mm2, adj f3,f342,f344,f356
  f344: plane 2.39x0.76mm, normal (0.96,-0.28,0), area 1.9mm2, adj f3,f343,f345,f356
  f345: extruded ~0.96x0.76mm, area 0.8mm2, adj f3,f344,f346,f356
  f346: extruded ~0.92x0.76mm, area 0.7mm2, adj f3,f345,f347,f356
  f347: plane 2.42x0.76mm, normal (-0.97,-0.25,0), area 1.9mm2, adj f3,f346,f348,f356
  f348: plane 0.76x0.48mm, normal (0,-1,0), area 0.4mm2, adj f3,f347,f349,f356
  f349: plane 3.92x1.04mm, normal (0.97,0.26,0), area 3.1mm2, adj f3,f348,f350,f356
  f350: plane 0.76x0.45mm, normal (0,1,0), area 0.3mm2, adj f3,f349,f351,f356
  f351: plane 2.61x0.77mm, normal (-0.96,0.28,0), area 2.1mm2, adj f3,f350,f352,f356
  f352: extruded ~0.78x0.76mm, area 0.6mm2, adj f3,f351,f353,f356
  f353: extruded ~0.76x0.32mm, area 0.2mm2, adj f3,f352,f354,f356
  f354: extruded ~0.76x0.44mm, area 0.3mm2, adj f3,f353,f355,f356
  f355: plane 2.63x0.79mm, normal (0.96,0.29,0), area 2.1mm2, adj f3,f336,f354,f356
  f356: plane 4.94x3.92mm, normal (0,0,1), area 6.6mm2, adj f336,f337,f338,f339,f340,f341,f342,f343
  f357: plane 1.45x1.13mm, normal (0,0,1), area 1.3mm2, adj f308,f309,f310,f311,f312,f313,f314,f334
  f358: cylinder r=5.56mm len=22.23mm, axis (-1,0,0), area 302.8mm2, adj f0,f1,f359,f360
  f359: bspline ~22.91x12.85mm, area 362.2mm2, adj f0,f1,f2,f358
  f360: bspline ~22.91x12.85mm, area 362.2mm2, adj f0,f1,f2,f358
PART D: 13 faces, bbox 162.6x17.4x17.4 mm
  f0: cylinder r=7.94mm len=15.88mm, axis (1,0,0), area 411.3mm2, adj f8,f9,f11,f12
  f1: plane 13.06x13.06mm, normal (-1,0,0), area 46.7mm2, adj f3,f4,f5,f6,f9
  f2: plane 10.62x10.49mm, normal (-1,0,0), area 82.5mm2, adj f3,f4,f5,f6
  f3: bspline ~149.91x12.85mm, area 2435.3mm2, adj f1,f2,f5,f6
  f4: bspline ~149.91x12.85mm, area 2437mm2, adj f1,f2,f5,f6
  f5: cylinder r=5.56mm len=149.23mm, axis (-1,0,0), area 3399mm2, adj f1,f2,f3,f4
  f6: cylinder r=4.67mm len=149.23mm, axis (-1,0,0), area 3537.3mm2, adj f1,f2,f3,f4
  f7: plane 12.83x12.83mm, normal (1,0,0), area 129.2mm2, adj f8
  f8: torus R=6.41mm, axis (1,0,0), area 111.1mm2, adj f0,f7
  f9: torus R=6.41mm, axis (1,0,0), area 111.1mm2, adj f0,f1
  f10: cylinder r=2.37mm len=14.35mm, axis (0,0,1), area 203.5mm2, adj f11,f12
  f11: bspline ~6.95x6.28mm, area 23.6mm2, adj f0,f10
  f12: bspline ~6.95x6.28mm, area 23.6mm2, adj f0,f10
PLACE A rot(axis=(1,0,0),49.5deg) t=(-12.77,-32.56,-51.7)mm
PLACE B rot(axis=(1,0,0),148.2deg) t=(-12.77,5.53,-45.77)mm
PLACE C t=(-26.4,-41.46,-32.39)mm fixed
PLACE D rot(axis=(1,0,0),49.5deg) t=(-12.77,-32.56,-51.7)mm
MATE planar D.f10 <-> A.f0  axis (0,-0.76,0.65) through (98.35,-16.06,-32.39)mm
MATE planar B.f6 <-> D.f0  axis (1,0,0) through (-57.22,-16.06,-32.39)mm
MATE cylindrical B.f6 <-> D.f0  axis (-1,0,0) through (-57.6,-16.06,-32.39)mm
MATE cylindrical D.f0 <-> C.f25  axis (1,0,0) through (98.35,-16.06,-32.39)mm
MATE cylindrical A.f0 <-> D.f10  axis (0,0.76,-0.65) through (98.35,-16.06,-32.39)mm
